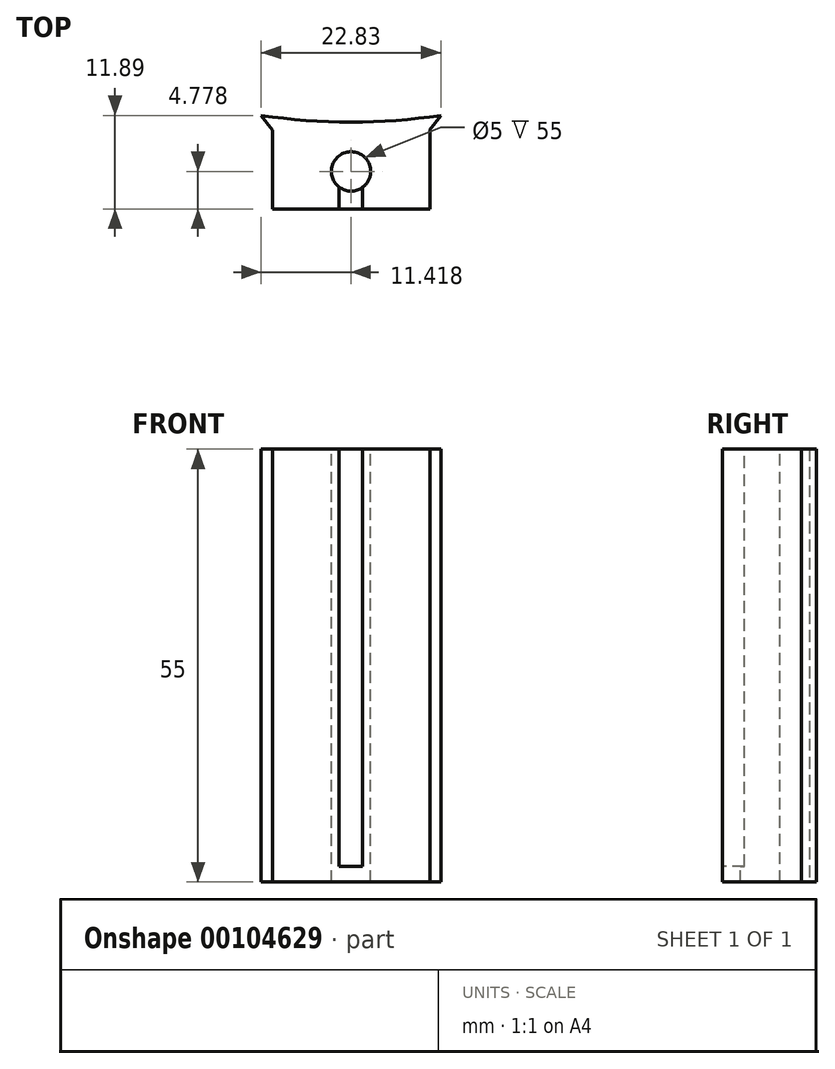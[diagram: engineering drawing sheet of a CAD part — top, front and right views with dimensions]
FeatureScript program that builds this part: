
annotation { "Feature Type Name" : "Feature", "Feature Type Description" : "" }
export const myFeature = defineFeature(function(context is Context, id is Id, definition is map)
    precondition{}
    {
        {
            var Q0;
            Q0=qCreatedBy(makeId("Top.planeOp"),FACE);
            var sketch = newSketch(context, id + "F0", { "sketchPlane" : qUnion([Q0])});
            skLineSegment(sketch, "E0.bottom", {"start": v(-24.83, 28.45) * mm, "end": v(-4.83, 28.45) * mm});
            skLineSegment(sketch, "E0.top", {"start": v(-24.83, 18.45) * mm, "end": v(-4.83, 18.45) * mm});
            skLineSegment(sketch, "E0.left", {"start": v(-24.83, 28.45) * mm, "end": v(-24.83, 18.45) * mm});
            skLineSegment(sketch, "E0.right", {"start": v(-4.83, 28.45) * mm, "end": v(-4.83, 18.45) * mm});
            skLineSegment(sketch, "E1.top", {"start": v(-26.33, 30.45) * mm, "end": v(-3.33, 30.45) * mm});
            skLineSegment(sketch, "E1.left", {"start": v(-24.83, 28.45) * mm, "end": v(-26.33, 30.45) * mm});
            skLineSegment(sketch, "E1.right", {"start": v(-4.83, 28.45) * mm, "end": v(-3.33, 30.45) * mm});
            skSolve(sketch);
        }
        {
            var Q0;
            Q0=qCreatedBy(makeId("Top.planeOp"),FACE);
            var sketch = newSketch(context, id + "F1", { "sketchPlane" : qUnion([Q0])});
            skCircle(sketch, "E2", {"center": v(-14.83, 107.78) * mm, "radius": 78.28 * mm});
            skSolve(sketch);
        }
        {
            var Q0;
            {var subQ1=sQuery(id+"F0.wireOp",EDGE,"E0.bottom");Q0=makeQuery(id+"F0.imprint","IMPRINT",FACE,{"disambiguationData":[TD([[makeQuery(id+"F0.imprint","IMPRINT",EDGE,{"derivedFrom":subQ1}),-1.0]])]});}
            var Q1;
            Q1=makeQuery(id+"F0.imprint","IMPRINT",FACE,{"disambiguationData":[TD([[makeQuery(id+"F0.imprint","IMPRINT",EDGE,{"derivedFrom":sQuery(id+"F0.wireOp",EDGE,"E1.top")}),-1.0]])]});
            extrude(context, id + "F2", {"entities" : qUnion([Q0, Q1]), "depth" : 55 * mm});
        }
        {
            var Q0;
            Q0=makeQuery(id+"F1.imprint","IMPRINT",FACE,{"disambiguationData":[TD([[makeQuery(id+"F1.imprint","IMPRINT",EDGE,{"derivedFrom":sQuery(id+"F1.wireOp",EDGE,"E2")}),1.0]])]});
            extrude(context, id + "F3", {"entities" : qUnion([Q0]), "operationType" : NewBodyOperationType.REMOVE, "depth" : 60 * mm});
        }
        {
            var Q0;
            Q0=makeQuery(id+"F2.opExtrude","CAP_FACE",FACE,{"disambiguationData":[OSD([sQuery(id+"F0.wireOp",EDGE,"E0.bottom"),sQuery(id+"F0.wireOp",EDGE,"E0.top"),sQuery(id+"F0.wireOp",EDGE,"E0.left"),sQuery(id+"F0.wireOp",EDGE,"E0.right"),sQuery(id+"F0.wireOp",EDGE,"E0.bottom"),sQuery(id+"F0.wireOp",EDGE,"E1.top"),sQuery(id+"F0.wireOp",EDGE,"E1.left"),sQuery(id+"F0.wireOp",EDGE,"E1.right")])],"isStart":false});
            var sketch = newSketch(context, id + "F4", { "sketchPlane" : qUnion([Q0])});
            skCircle(sketch, "E3", {"center": v(-14.83, 23.23) * mm, "radius": 2.5 * mm});
            skLineSegment(sketch, "E4.bottom", {"start": v(-16.34, 21.24) * mm, "end": v(-13.34, 21.24) * mm});
            skLineSegment(sketch, "E4.top", {"start": v(-16.34, 18.45) * mm, "end": v(-13.34, 18.45) * mm});
            skLineSegment(sketch, "E4.left", {"start": v(-16.34, 21.24) * mm, "end": v(-16.34, 18.45) * mm});
            skLineSegment(sketch, "E4.right", {"start": v(-13.34, 21.24) * mm, "end": v(-13.34, 18.45) * mm});
            skSolve(sketch);
        }
        {
            var Q0;
            {var subQ0=sQuery(id+"F4.wireOp",EDGE,"E4.bottom");Q0=makeQuery(id+"F4.imprint","IMPRINT",FACE,{"disambiguationData":[TD([[makeQuery(id+"F4.imprint","IMPRINT",EDGE,{"derivedFrom":subQ0}),1.0]])]});}
            var Q1;
            {var subQ0=sQuery(id+"F4.wireOp",EDGE,"E4.bottom");Q1=makeQuery(id+"F4.imprint","IMPRINT",FACE,{"disambiguationData":[TD([[makeQuery(id+"F4.imprint","IMPRINT",EDGE,{"derivedFrom":subQ0}),-1.0]])]});}
            extrude(context, id + "F5", {"entities" : qUnion([Q0, Q1]), "operationType" : NewBodyOperationType.REMOVE, "oppositeDirection" : true, "depth" : 60 * mm});
        }
        {
            var Q0;
            {var subQ4=sQuery(id+"F4.wireOp",EDGE,"E4.top");Q0=makeQuery(id+"F4.imprint","IMPRINT",FACE,{"disambiguationData":[TD([[makeQuery(id+"F4.imprint","IMPRINT",EDGE,{"derivedFrom":subQ4}),1.0]])]});}
            extrude(context, id + "F6", {"entities" : qUnion([Q0]), "operationType" : NewBodyOperationType.REMOVE, "oppositeDirection" : true, "depth" : 53 * mm});
        }
    });
